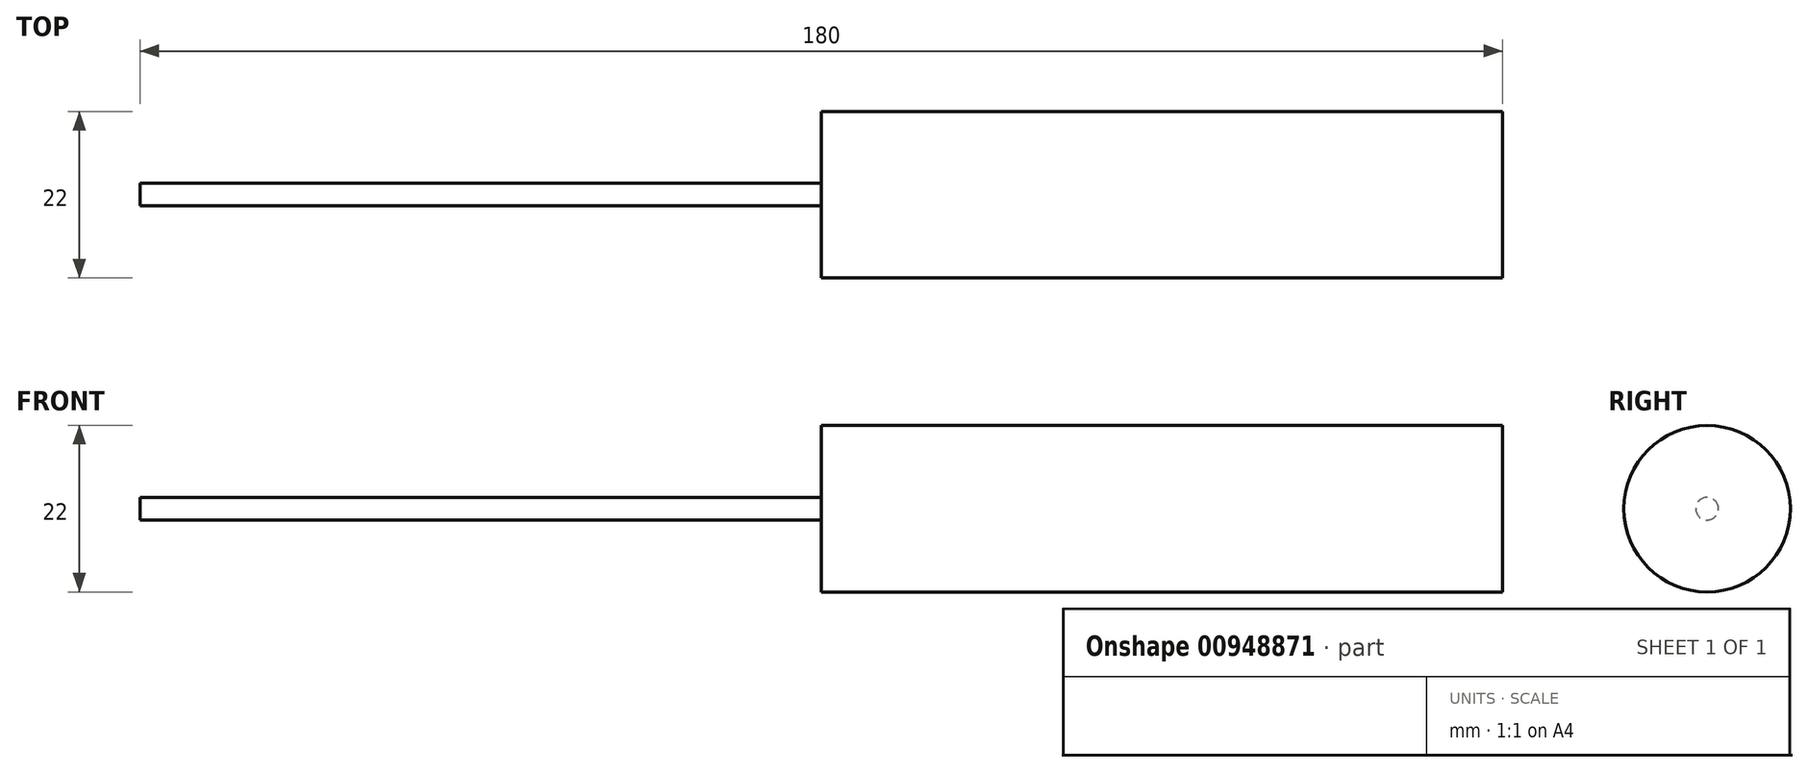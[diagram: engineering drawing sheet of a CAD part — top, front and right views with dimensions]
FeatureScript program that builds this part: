
annotation { "Feature Type Name" : "Feature", "Feature Type Description" : "" }
export const myFeature = defineFeature(function(context is Context, id is Id, definition is map)
    precondition{}
    {
        {
            var Q0;
            Q0=qCreatedBy(makeId("Front.planeOp"),FACE);
            var sketch = newSketch(context, id + "F0", { "sketchPlane" : qUnion([Q0])});
            skLineSegment(sketch, "E0", {"start": v(0, 0) * mm, "end": v(0, 11) * mm});
            skLineSegment(sketch, "E1", {"start": v(0, 11) * mm, "end": v(-90, 11) * mm});
            skLineSegment(sketch, "E2", {"start": v(-90, 11) * mm, "end": v(-90, 1.5) * mm});
            skLineSegment(sketch, "E3", {"start": v(-90, 1.5) * mm, "end": v(-180, 1.5) * mm});
            skLineSegment(sketch, "E4", {"start": v(-180, 1.5) * mm, "end": v(-180, 0) * mm});
            skLineSegment(sketch, "E5", {"start": v(-180, 0) * mm, "end": v(0, 0) * mm});
            skSolve(sketch);
        }
        {
            var Q0;
            Q0=makeQuery(id+"F0.imprint","IMPRINT",FACE,{"disambiguationData":[TD([[makeQuery(id+"F0.imprint","IMPRINT",EDGE,{"derivedFrom":sQuery(id+"F0.wireOp",EDGE,"E0")}),1.0]])]});
            var Q1;
            Q1=sQuery(id+"F0.wireOp",EDGE,"E5");
            revolve(context, id + "F1", {"surfaceOperationType" : NewSurfaceOperationType.NEW, "entities" : qUnion([Q0]), "axis" : qUnion([Q1]), "revolveType" : RevolveType.FULL});
        }
    });
